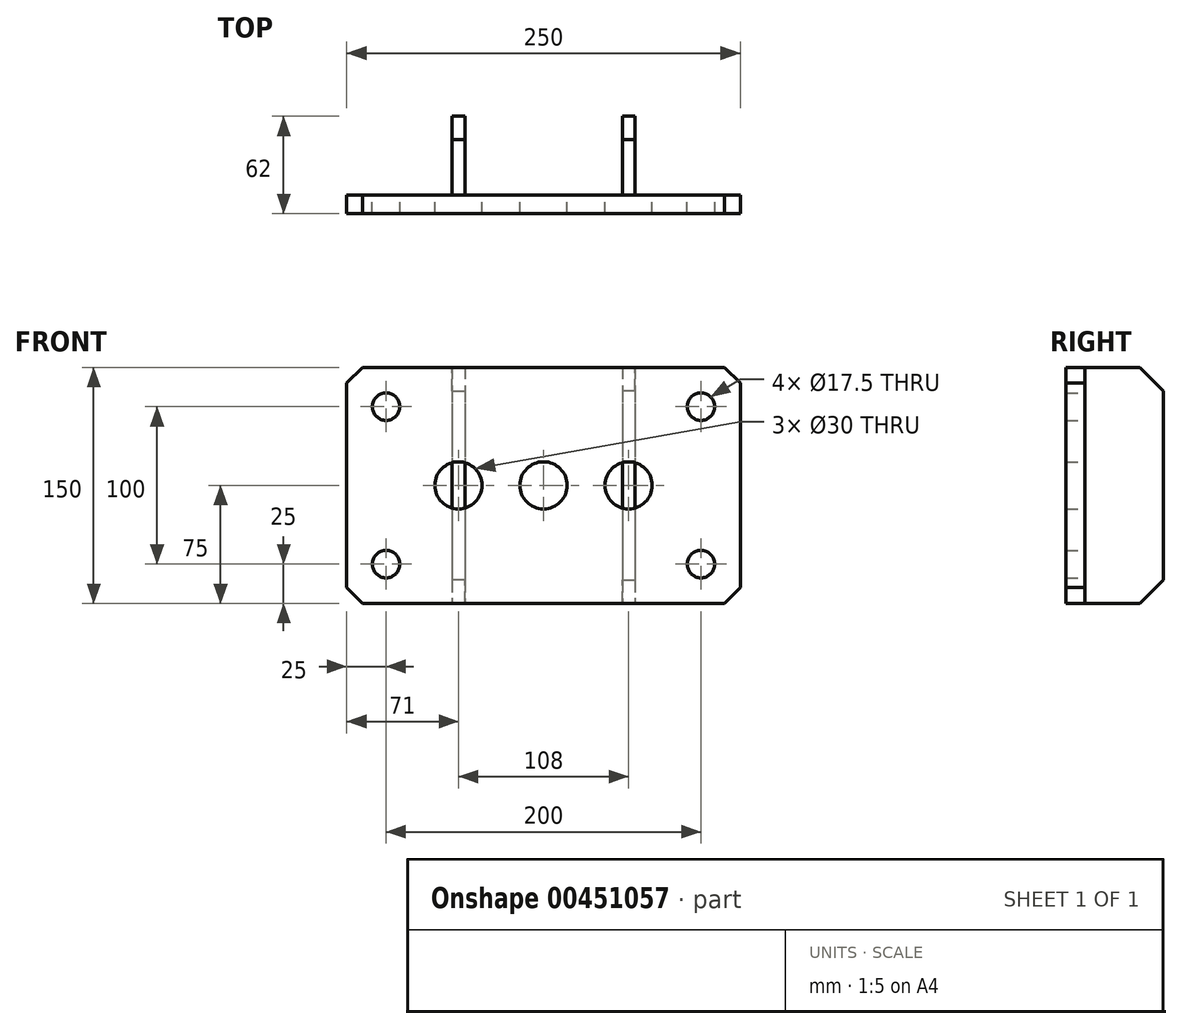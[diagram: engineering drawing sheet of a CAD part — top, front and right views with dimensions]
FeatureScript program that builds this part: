
annotation { "Feature Type Name" : "Feature", "Feature Type Description" : "" }
export const myFeature = defineFeature(function(context is Context, id is Id, definition is map)
    precondition{}
    {
        {
            var Q0;
            Q0=qCreatedBy(makeId("Front.planeOp"),FACE);
            var sketch = newSketch(context, id + "F0", { "sketchPlane" : qUnion([Q0])});
            skLineSegment(sketch, "E0.bottom", {"start": v(125, 75) * mm, "end": v(-125, 75) * mm});
            skLineSegment(sketch, "E0.top", {"start": v(125, -75) * mm, "end": v(-125, -75) * mm});
            skLineSegment(sketch, "E0.left", {"start": v(125, 75) * mm, "end": v(125, -75) * mm});
            skLineSegment(sketch, "E0.right", {"start": v(-125, 75) * mm, "end": v(-125, -75) * mm});
            skPoint(sketch, "E0.middle", {"position": v(0, 0) * mm});
            skSolve(sketch);
        }
        {
            var Q0;
            Q0 = qSketchRegion(id + "F0", true);
            extrude(context, id + "F1", {"entities" : qUnion([Q0]), "depth" : 12 * mm, "symmetric" : true});
        }
        {
            var Q0;
            Q0=makeQuery(id+"F1.opExtrude","SWEPT_EDGE",EDGE,{"disambiguationData":[OSD([sQuery(id+"F0.wireOp",EDGE,"E0.top"),sQuery(id+"F0.wireOp",EDGE,"E0.left")])]});
            var Q1;
            Q1=makeQuery(id+"F1.opExtrude","SWEPT_EDGE",EDGE,{"disambiguationData":[OSD([sQuery(id+"F0.wireOp",EDGE,"E0.bottom"),sQuery(id+"F0.wireOp",EDGE,"E0.right")])]});
            var Q2;
            Q2=makeQuery(id+"F1.opExtrude","SWEPT_EDGE",EDGE,{"disambiguationData":[OSD([sQuery(id+"F0.wireOp",EDGE,"E0.bottom"),sQuery(id+"F0.wireOp",EDGE,"E0.left")])]});
            var Q3;
            Q3=makeQuery(id+"F1.opExtrude","SWEPT_EDGE",EDGE,{"disambiguationData":[OSD([sQuery(id+"F0.wireOp",EDGE,"E0.top"),sQuery(id+"F0.wireOp",EDGE,"E0.right")])]});
            chamfer(context, id + "F2", {"entities" : qUnion([Q0, Q1, Q2, Q3]), "width" : 10 * mm, "tangentPropagation" : true});
        }
        {
            var Q0;
            Q0=makeQuery(id+"F1.opExtrude","CAP_FACE",FACE,{"disambiguationData":[OSD([sQuery(id+"F0.wireOp",EDGE,"E0.bottom"),sQuery(id+"F0.wireOp",EDGE,"E0.top"),sQuery(id+"F0.wireOp",EDGE,"E0.left"),sQuery(id+"F0.wireOp",EDGE,"E0.right")])],"isStart":false});
            var sketch = newSketch(context, id + "F3", { "sketchPlane" : qUnion([Q0])});
            skPoint(sketch, "E1", {"position": v(-100, -50) * mm});
            skLineSegment(sketch, "E2", {"start": v(-57.28, 0) * mm, "end": v(55.56, 0) * mm});
            skLineSegment(sketch, "E3", {"start": v(0, 42.21) * mm, "end": v(0, -33.12) * mm});
            skPoint(sketch, "E4.MirrorP", {"position": v(-100, 50) * mm});
            skPoint(sketch, "E5.MirrorP", {"position": v(100, 50) * mm});
            skPoint(sketch, "E6.MirrorP", {"position": v(100, -50) * mm});
            skSolve(sketch);
        }
        {
            var Q0;
            Q0=sQuery(id+"F3.wireOp",VERTEX,"E4.MirrorP");
            var Q1;
            Q1=sQuery(id+"F3.wireOp",VERTEX,"E1");
            var Q2;
            Q2=sQuery(id+"F3.wireOp",VERTEX,"E6.MirrorP");
            var Q3;
            Q3=sQuery(id+"F3.wireOp",VERTEX,"E5.MirrorP");
            var Q4;
            Q4=makeQuery(id+"F1.opExtrude","SWEPT_BODY",BODY,{"disambiguationData":[OSD([sQuery(id+"F0.wireOp",EDGE,"E0.bottom"),sQuery(id+"F0.wireOp",EDGE,"E0.top"),sQuery(id+"F0.wireOp",EDGE,"E0.left"),sQuery(id+"F0.wireOp",EDGE,"E0.right")])]});
            hole(context, id + "F4", {"style" : HoleStyle.SIMPLE, "endStyle" : HoleEndStyle.THROUGH, "standardTappedOrClearance" : lookupTablePath({ "standard" : "ISO", "fit" : "Normal", "size" : "M16", "type" : "Clearance" }), "standardBlindInLast" : lookupTablePath({ "fit" : "Standard", "standard" : "ISO", "size" : "M16", "type" : "Clearance" }), "holeDiameter" : 17.5 * mm, "isTappedThrough" : true, "tappedDepth" : 12 * mm, "tapClearance" : 3, "locations" : qUnion([Q0, Q1, Q2, Q3]), "scope" : qUnion([Q4])});
        }
        {
            var Q0;
            Q0=makeQuery(id+"F1.opExtrude","CAP_FACE",FACE,{"disambiguationData":[OSD([sQuery(id+"F0.wireOp",EDGE,"E0.bottom"),sQuery(id+"F0.wireOp",EDGE,"E0.top"),sQuery(id+"F0.wireOp",EDGE,"E0.left"),sQuery(id+"F0.wireOp",EDGE,"E0.right")])],"isStart":false});
            var sketch = newSketch(context, id + "F5", { "sketchPlane" : qUnion([Q0])});
            skPoint(sketch, "E7", {"position": v(0, 0) * mm});
            skPoint(sketch, "E8", {"position": v(-54, 0) * mm});
            skPoint(sketch, "E9", {"position": v(54, 0) * mm});
            skLineSegment(sketch, "E10", {"start": v(-54, 0) * mm, "end": v(54, 0) * mm, "construction": true});
            skSolve(sketch);
        }
        {
            var Q0;
            Q0=sQuery(id+"F5.wireOp",VERTEX,"E7");
            var Q1;
            Q1=sQuery(id+"F5.wireOp",VERTEX,"E8");
            var Q2;
            Q2=sQuery(id+"F5.wireOp",VERTEX,"E9");
            var Q3;
            Q3=makeQuery(id+"F1.opExtrude","SWEPT_BODY",BODY,{"disambiguationData":[OSD([sQuery(id+"F0.wireOp",EDGE,"E0.bottom"),sQuery(id+"F0.wireOp",EDGE,"E0.top"),sQuery(id+"F0.wireOp",EDGE,"E0.left"),sQuery(id+"F0.wireOp",EDGE,"E0.right")])]});
            hole(context, id + "F6", {"style" : HoleStyle.SIMPLE, "endStyle" : HoleEndStyle.THROUGH, "holeDiameter" : 30 * mm, "isTappedThrough" : true, "tappedDepth" : 12 * mm, "tapClearance" : 3, "locations" : qUnion([Q0, Q1, Q2]), "scope" : qUnion([Q3])});
        }
        {
            var Q0;
            Q0=makeQuery(id+"F1.opExtrude","CAP_FACE",FACE,{"disambiguationData":[OSD([sQuery(id+"F0.wireOp",EDGE,"E0.bottom"),sQuery(id+"F0.wireOp",EDGE,"E0.top"),sQuery(id+"F0.wireOp",EDGE,"E0.left"),sQuery(id+"F0.wireOp",EDGE,"E0.right")])],"isStart":true});
            var sketch = newSketch(context, id + "F7", { "sketchPlane" : qUnion([Q0])});
            skLineSegment(sketch, "E11.bottom", {"start": v(50, 75) * mm, "end": v(58, 75) * mm});
            skLineSegment(sketch, "E11.top", {"start": v(50, -75) * mm, "end": v(58, -75) * mm});
            skLineSegment(sketch, "E11.left", {"start": v(50, 75) * mm, "end": v(50, -75) * mm});
            skLineSegment(sketch, "E11.right", {"start": v(58, 75) * mm, "end": v(58, -75) * mm});
            skSolve(sketch);
        }
        {
            var Q0;
            Q0 = qSketchRegion(id + "F7", true);
            extrude(context, id + "F8", {"entities" : qUnion([Q0]), "depth" : 50 * mm});
        }
        {
            var Q0;
            Q0=makeQuery(id+"F8.opExtrude","CAP_EDGE",EDGE,{"disambiguationData":[OSD([sQuery(id+"F7.wireOp",EDGE,"E11.top")])],"isStart":false});
            var Q1;
            Q1=makeQuery(id+"F8.opExtrude","CAP_EDGE",EDGE,{"disambiguationData":[OSD([sQuery(id+"F7.wireOp",EDGE,"E11.bottom")])],"isStart":false});
            chamfer(context, id + "F9", {"entities" : qUnion([Q0, Q1]), "width" : 15 * mm, "tangentPropagation" : true});
        }
        {
            var Q0;
            Q0=makeQuery(id+"F8.opExtrude","SWEPT_BODY",BODY,{"disambiguationData":[OSD([sQuery(id+"F7.wireOp",EDGE,"E11.bottom"),sQuery(id+"F7.wireOp",EDGE,"E11.top"),sQuery(id+"F7.wireOp",EDGE,"E11.left"),sQuery(id+"F7.wireOp",EDGE,"E11.right")])]});
            var Q1;
            Q1=qCreatedBy(makeId("Right.planeOp"),FACE);
            mirror(context, id + "F10", {"entities" : qUnion([Q0]), "mirrorPlane" : qUnion([Q1])});
        }
    });
